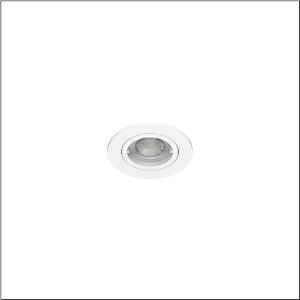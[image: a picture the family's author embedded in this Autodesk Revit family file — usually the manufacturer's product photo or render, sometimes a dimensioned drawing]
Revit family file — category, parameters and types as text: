
# Revit family: lunis_41_spot_51dt137a31a
name_source: partatom
category: Lighting Fixtures
units: mm (PartAtom-declared; Revit-internal decimal feet)

## family parameters
Cut with Voids When Loaded = No
Host = Face
Light Source = No
Part Type = Normal
Room Calculation Point = No
Round Connector Dimension = Use Diameter
Shared = No

## types (1)
- Lunis 41 Spot (1 x LED, 500 lm, 5 W, 3000K)
    Apparent Load = 5 VA
    CIE Flux Codes = 87 97 99 100 100
    Color Rendering = 80
    Color Temperature = 3000K
    Default Elevation = 1800 mm
    Description = Lunis 41,  Spot, downlight, light emission: direct distribution, LED rated luminous flux: 500lm, light colour: 830, control gear: ECG, mains connection: 230V, AC, 50/60Hz, housing, round, of aluminium, coated, traffic white (RAL 9016), diameter: 88mm, recess depth: 54mm, protection rating (complete): IP20, protection rating (on room side): IP20, insulation class (complete): insulation class II (safety insulation), certification: CE, permissible ambient temperature for indoor applications: -20..+40°C, packaging unit: 1 piece
    Height = 0 mm  [stored 0 ft]
    Lamp = 1 x LED
    Lamp Light Flux = 500 lm
    Lamp Power = 5 W
    Lamp count = 1
    Length = 88 mm
    Luminous efficacy = 100 lm/W
    Manufacturer = Siteco
    ModVariant = No
    Model = 51DT137A31A
    Mounting Place = Ceiling
    Mounting Type = Recessed
    Number of Poles = 1
    OnlyDefault = Yes
    Power Factor = 1
    Product Name = Lunis 41 Spot
    Product group = downlight
    ProductGroupID = 400
    Protection Class = Protection class II
    Protection Degree = IP 20
    RLX_Detail_Level = 1
    RLX_Emergency_Light_Flux = 0 lm
    RLX_Emergency_Type = 0
    RLX_Emergency_Type_DB = No
    RlxData = <blob elided: 38021 chars, md5=5a5aa3a3>
    Socket = socket
    Standby Power = 0 W
    System Light Flux = 500 lm
    System Power = 5 W
    Type Comments = Product without accessories
    Type Image = l_1005286.jpg
    URL = http://relux.com
    VarID = ---
    Voltage = 0 V
    Weight = 0.00 kg
    Width = 0 mm  [stored 0 ft]

note: [stored X ft] marks values corroborated as IEEE doubles in the binary element streams (Revit-internal decimal feet)

## geometry (parser evidence)
native form markers: Blend x4, Sweep x11
no freeform markers — native parametric forms only
